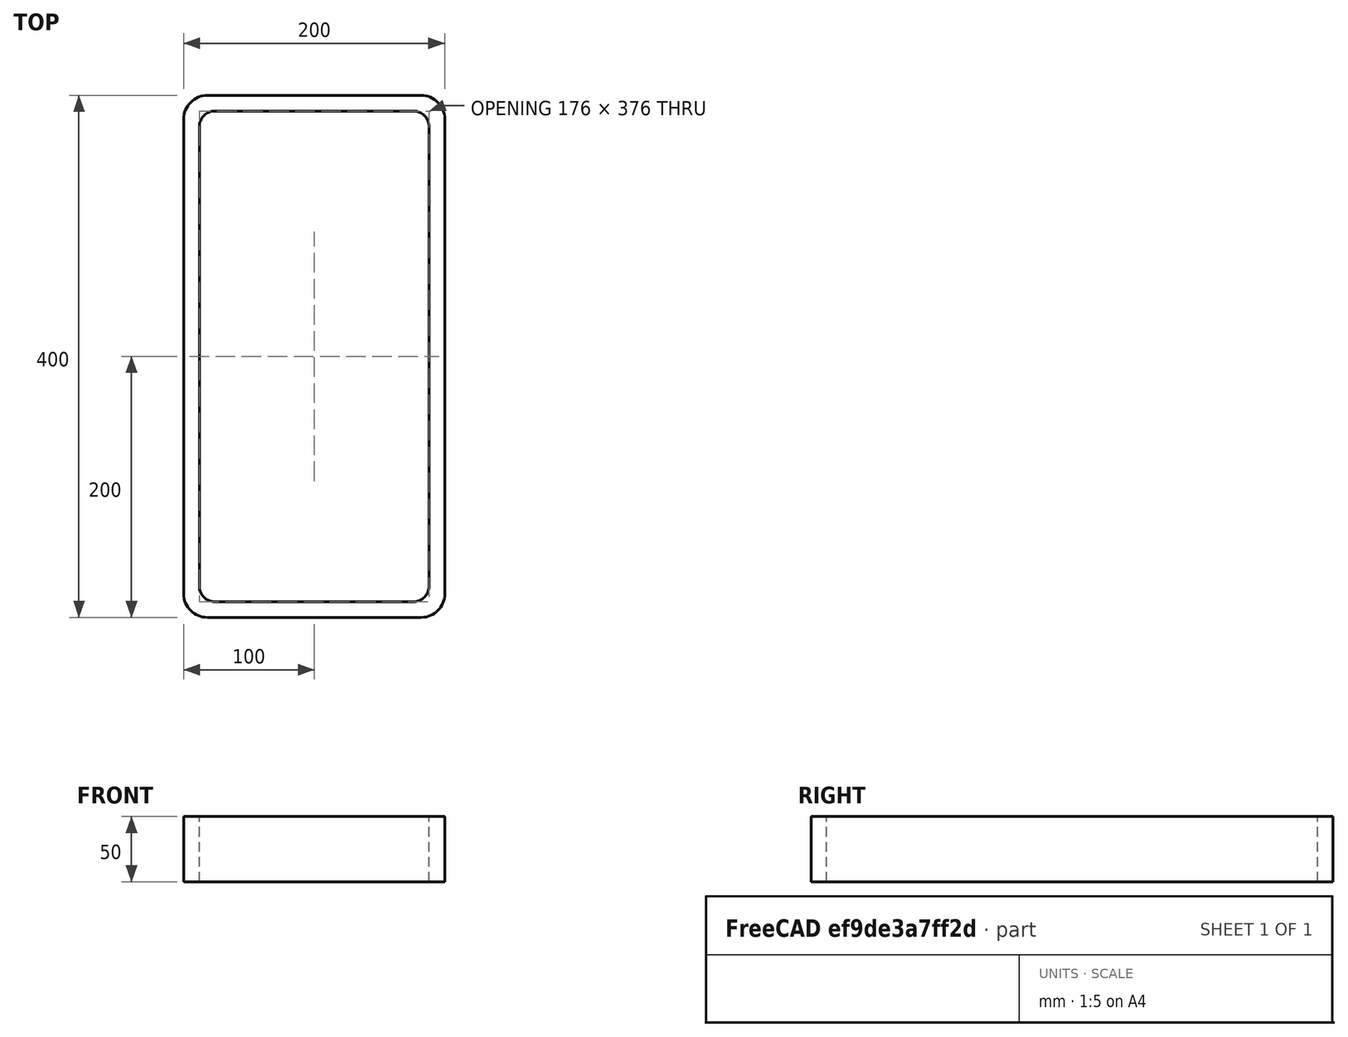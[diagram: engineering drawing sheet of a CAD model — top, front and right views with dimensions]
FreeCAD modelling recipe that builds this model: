
FCSTD DOCUMENT  (FreeCAD 0.15R4671 (Git))
Label: Rectangular hollow section 400x200x12 EN10219 S235JRH
License: All rights reserved
LicenseURL: http://en.wikipedia.org/wiki/All_rights_reserved
objects: Sketcher::SketchObject×1, Part::Extrusion×1
note: 2 computed .brp shape members not serialized (recipe doc carries the construction recipe); baked Part::Feature solids carry a one-line shape summary decoded from their .brp

FEATURE [Sketcher::SketchObject] Sketch
  sketch-geometry (16):
    g0: LineSegment StartX=-76 StartY=188 StartZ=0 EndX=76 EndY=188 EndZ=0
    g1: LineSegment StartX=88 StartY=176 StartZ=0 EndX=88 EndY=-176 EndZ=0
    g2: LineSegment StartX=76 StartY=-188 StartZ=0 EndX=-76 EndY=-188 EndZ=0
    g3: LineSegment StartX=-88 StartY=-176 StartZ=0 EndX=-88 EndY=176 EndZ=0
    g4: LineSegment StartX=-82 StartY=200 StartZ=0 EndX=82 EndY=200 EndZ=0
    g5: LineSegment StartX=100 StartY=182 StartZ=0 EndX=100 EndY=-182 EndZ=0
    g6: LineSegment StartX=82 StartY=-200 StartZ=0 EndX=-82 EndY=-200 EndZ=0
    g7: LineSegment StartX=-100 StartY=-182 StartZ=0 EndX=-100 EndY=182 EndZ=0
    g8: ArcOfCircle CenterX=-76 CenterY=176 CenterZ=0 NormalX=0 NormalY=0 NormalZ=1 Radius=12 StartAngle=1.5708 EndAngle=3.14159
    g9: ArcOfCircle CenterX=76 CenterY=176 CenterZ=0 NormalX=0 NormalY=0 NormalZ=1 Radius=12 StartAngle=0 EndAngle=1.5708
    g10: ArcOfCircle CenterX=76 CenterY=-176 CenterZ=0 NormalX=0 NormalY=0 NormalZ=1 Radius=12 StartAngle=4.71239 EndAngle=6.28319
    g11: ArcOfCircle CenterX=-76 CenterY=-176 CenterZ=0 NormalX=0 NormalY=0 NormalZ=1 Radius=12 StartAngle=3.14159 EndAngle=4.71239
    g12: ArcOfCircle CenterX=82 CenterY=182 CenterZ=0 NormalX=0 NormalY=0 NormalZ=1 Radius=18 StartAngle=0 EndAngle=1.5708
    g13: ArcOfCircle CenterX=82 CenterY=-182 CenterZ=0 NormalX=0 NormalY=0 NormalZ=1 Radius=18 StartAngle=4.71239 EndAngle=6.28319
    g14: ArcOfCircle CenterX=-82 CenterY=-182 CenterZ=0 NormalX=0 NormalY=0 NormalZ=1 Radius=18 StartAngle=3.14159 EndAngle=4.71239
    g15: ArcOfCircle CenterX=-82 CenterY=182 CenterZ=0 NormalX=0 NormalY=0 NormalZ=1 Radius=18 StartAngle=1.5708 EndAngle=3.14159
  constraints (36):
    c: Horizontal(g2)
    c: Vertical(g3)
    c: Horizontal(g6)
    c: Vertical(g7)
    c: Tangent(g3,g8) = 1.5708
    c: Tangent(g0,g8) = 1.5708
    c: Tangent(g0,g9) = 1.5708
    c: Tangent(g1,g9) = 1.5708
    c: Tangent(g1,g10) = 1.5708
    c: Tangent(g2,g10) = 1.5708
    c: Tangent(g2,g11) = 1.5708
    c: Tangent(g3,g11) = 1.5708
    c: Tangent(g4,g12) = 1.5708
    c: Tangent(g5,g12) = 1.5708
    c: Tangent(g5,g13) = 1.5708
    c: Tangent(g6,g13) = 1.5708
    c: Tangent(g6,g14) = 1.5708
    c: Tangent(g7,g14) = 1.5708
    c: Tangent(g7,g15) = 1.5708
    c: Tangent(g4,g15) = 1.5708
    c: Equal(g9,g8)
    c: Equal(g9,g11)
    c: Equal(g9,g10)
    c: Equal(g12,g15)
    c: Equal(g12,g14)
    c: Equal(g12,g13)
    c: Symmetric(g4,g6,g-1)
    c: Symmetric(g7,g5,g-2)
    c: DistanceY(g4,g6) = -400
    c: DistanceX(g7,g5) = 200
    c: Symmetric(g3,g1,g-2)
    c: Symmetric(g0,g2,g-1)
    c: DistanceY(g0,g4) = 12
    c: DistanceX(g5,g1) = -12
    c: Radius(g9) = 12
    c: Radius(g12) = 18
FEATURE [Part::Extrusion] Extrude  label="Rectangular hollow section 400x200x12 EN10219 S235JRH"
  Base = -> Sketch
  Dir = (0,0,50)
  Solid = true
